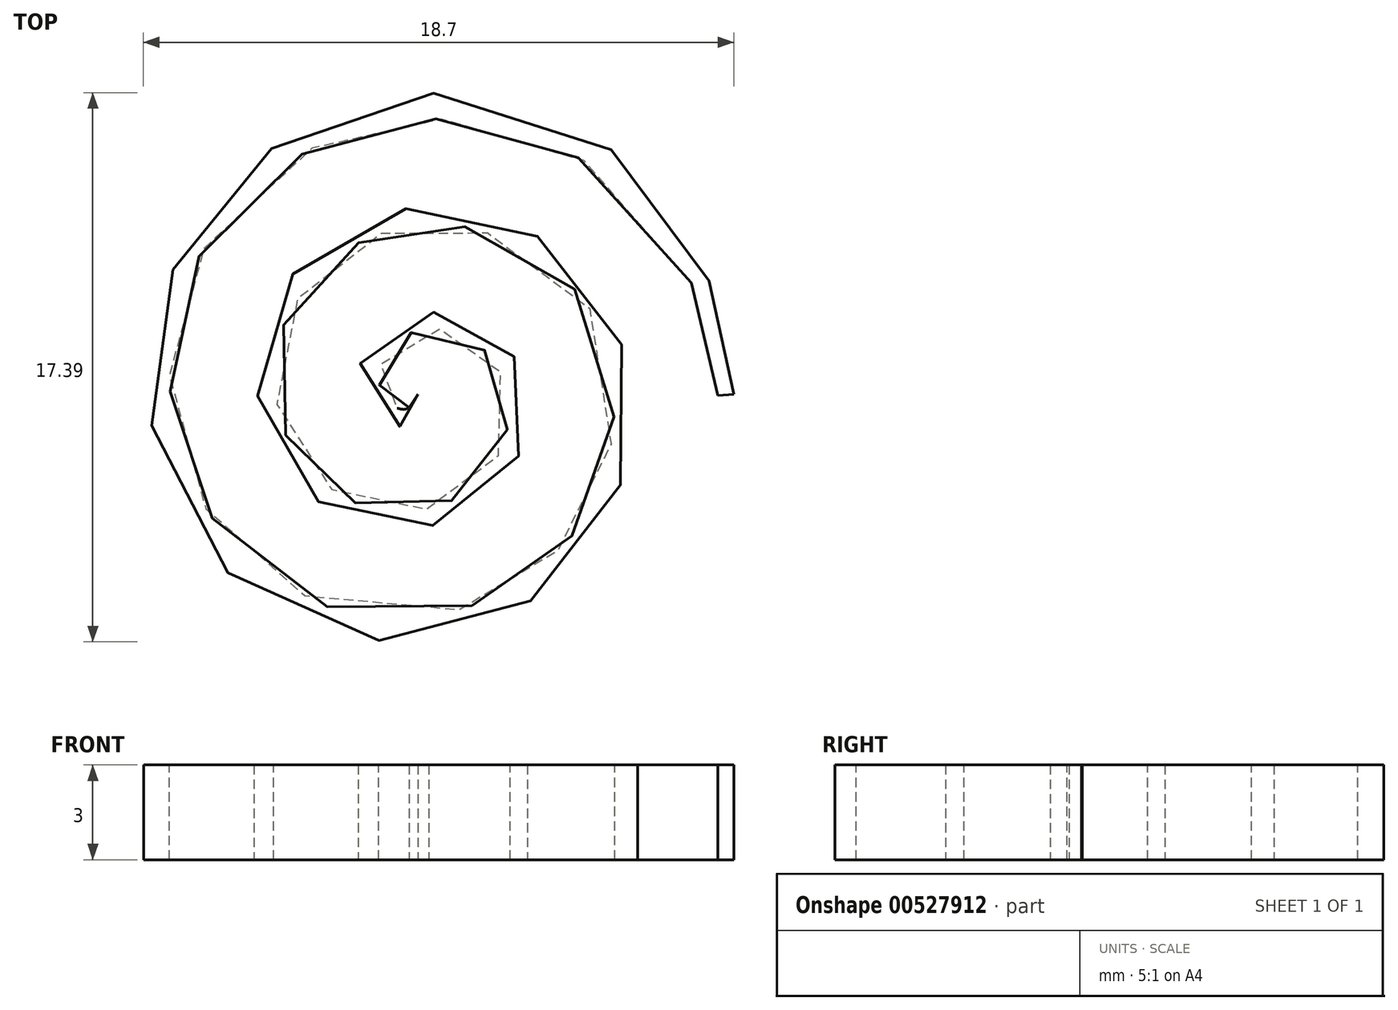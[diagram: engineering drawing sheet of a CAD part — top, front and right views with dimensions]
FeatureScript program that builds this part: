
annotation { "Feature Type Name" : "Feature", "Feature Type Description" : "" }
export const myFeature = defineFeature(function(context is Context, id is Id, definition is map)
    precondition{}
    {
        {
            var Q0;
            Q0=qCreatedBy(makeId("Top.planeOp"),FACE);
            var sketch = newSketch(context, id + "F0", { "sketchPlane" : qUnion([Q0])});
            skFitSpline(sketch, "E0", {"points": [v(10.28, 0.41) * mm, v(10.2, 1.9) * mm, v(9.79, 3.34) * mm, v(7.91, 6.78) * mm, v(5.9, 8.42) * mm, v(1.4, 9.87) * mm, v(-1.07, 9.69) * mm, v(-5.15, 7.73) * mm, v(-6.75, 5.97) * mm, v(-8.29, 1.93) * mm, v(-8.23, -0.34) * mm, v(-6.64, -4.14) * mm, v(-5.11, -5.67) * mm, v(-1.52, -7.25) * mm, v(0.52, -7.3) * mm, v(4.02, -6.03) * mm, v(5.46, -4.73) * mm, v(7.03, -1.58) * mm, v(7.16, 0.24) * mm, v(6.19, 3.41) * mm, v(5.1, 4.74) * mm, v(2.37, 6.26) * mm, v(0.77, 6.45) * mm, v(-2.05, 5.72) * mm, v(-3.25, 4.81) * mm, v(-4.68, 2.5) * mm, v(-4.9, 1.13) * mm, v(-4.37, -1.33) * mm, v(-3.64, -2.39) * mm, v(-1.72, -3.68) * mm, v(-0.56, -3.9) * mm, v(1.51, -3.54) * mm, v(2.42, -2.95) * mm, v(3.53, -1.4) * mm, v(3.74, -0.46) * mm, v(3.5, 1.23) * mm, v(3.04, 1.96) * mm, v(1.83, 2.86) * mm, v(1.1, 3.04) * mm, v(-0.2, 2.85) * mm, v(-0.75, 2.5) * mm, v(-1.53, 1.44) * mm, v(-1.55, 0.67) * mm, v(-1, -0.36) * mm, v(-0.48, -0.6) * mm, v(0.31, -0.5) * mm, v(0.57, -0.2) * mm, v(0.59, 0.26) * mm, v(0.44, 0.41) * mm, v(0.28, 0.41) * mm]});
            skFitSpline(sketch, "E1", {"points": [v(9.78, 0.39) * mm, v(9.74, 1.09) * mm, v(9.63, 1.78) * mm, v(9.2, 3.33) * mm, v(8.82, 4.16) * mm, v(7.4, 6.37) * mm, v(6.07, 7.53) * mm, v(3.74, 8.64) * mm, v(2.87, 8.9) * mm, v(1.1, 9.13) * mm, v(0.22, 9.11) * mm, v(-1.68, 8.8) * mm, v(-2.67, 8.43) * mm, v(-4.43, 7.38) * mm, v(-5.2, 6.7) * mm, v(-6.44, 5.13) * mm, v(-6.9, 4.26) * mm, v(-7.49, 2.42) * mm, v(-7.6, 1.46) * mm, v(-7.5, -0.4) * mm, v(-7.3, -1.3) * mm, v(-6.58, -2.95) * mm, v(-6.08, -3.7) * mm, v(-4.87, -4.97) * mm, v(-4.17, -5.49) * mm, v(-2.09, -6.52) * mm, v(-0.58, -6.73) * mm, v(1.5, -6.42) * mm, v(2.15, -6.21) * mm, v(3.35, -5.63) * mm, v(3.9, -5.25) * mm, v(4.97, -4.26) * mm, v(5.46, -3.61) * mm, v(6.16, -2.21) * mm, v(6.36, -1.45) * mm, v(6.5, 0.06) * mm, v(6.44, 0.82) * mm, v(5.9, 2.73) * mm, v(5.19, 3.8) * mm, v(3.76, 4.94) * mm, v(3.2, 5.25) * mm, v(2.03, 5.66) * mm, v(1.42, 5.76) * mm, v(0.24, 5.77) * mm, v(-0.33, 5.68) * mm, v(-1.39, 5.33) * mm, v(-1.88, 5.06) * mm, v(-2.83, 4.34) * mm, v(-3.27, 3.86) * mm, v(-3.9, 2.79) * mm, v(-4.1, 2.2) * mm, v(-4.28, 1) * mm, v(-4.25, 0.38) * mm, v(-3.95, -0.76) * mm, v(-3.69, -1.28) * mm, v(-3.05, -2.1) * mm, v(-2.7, -2.43) * mm, v(-1.94, -2.91) * mm, v(-1.52, -3.09) * mm, v(-0.58, -3.3) * mm, v(-0.06, -3.31) * mm, v(0.9, -3.14) * mm, v(1.35, -2.95) * mm, v(2.07, -2.46) * mm, v(2.35, -2.19) * mm, v(2.8, -1.57) * mm, v(2.95, -1.24) * mm, v(3.16, -0.48) * mm, v(3.18, -0.05) * mm, v(3.06, 0.73) * mm, v(2.91, 1.09) * mm, v(2.54, 1.65) * mm, v(2.33, 1.87) * mm, v(1.88, 2.2) * mm, v(1.63, 2.32) * mm, v(1.1, 2.46) * mm, v(0.83, 2.48) * mm, v(0.2, 2.42) * mm, v(-0.15, 2.26) * mm, v(-0.58, 1.9) * mm, v(-0.7, 1.75) * mm, v(-0.88, 1.42) * mm, v(-0.93, 1.25) * mm, v(-0.97, 0.9) * mm, v(-0.95, 0.72) * mm, v(-0.88, 0.45) * mm, v(-0.82, 0.36) * mm, v(-0.7, 0.19) * mm, v(-0.62, 0.12) * mm, v(-0.46, 0.01) * mm, v(-0.36, -0.03) * mm, v(-0.2, -0.06) * mm, v(-0.13, -0.05) * mm, v(-0.05, -0.03) * mm, v(-0.02, -0.01) * mm, v(0, 0) * mm]});
            skLineSegment(sketch, "E2", {"start": v(9.78, 0.39) * mm, "end": v(10.28, 0.41) * mm});
            skLineSegment(sketch, "E3", {"start": v(0, 0) * mm, "end": v(0.28, 0.41) * mm});
            skSolve(sketch);
        }
        {
            var Q0;
            Q0=qSketchRegion(id+"F0",true);
            extrude(context, id + "F1", {"entities" : qUnion([Q0]), "depth" : 3 * mm});
        }
    });
